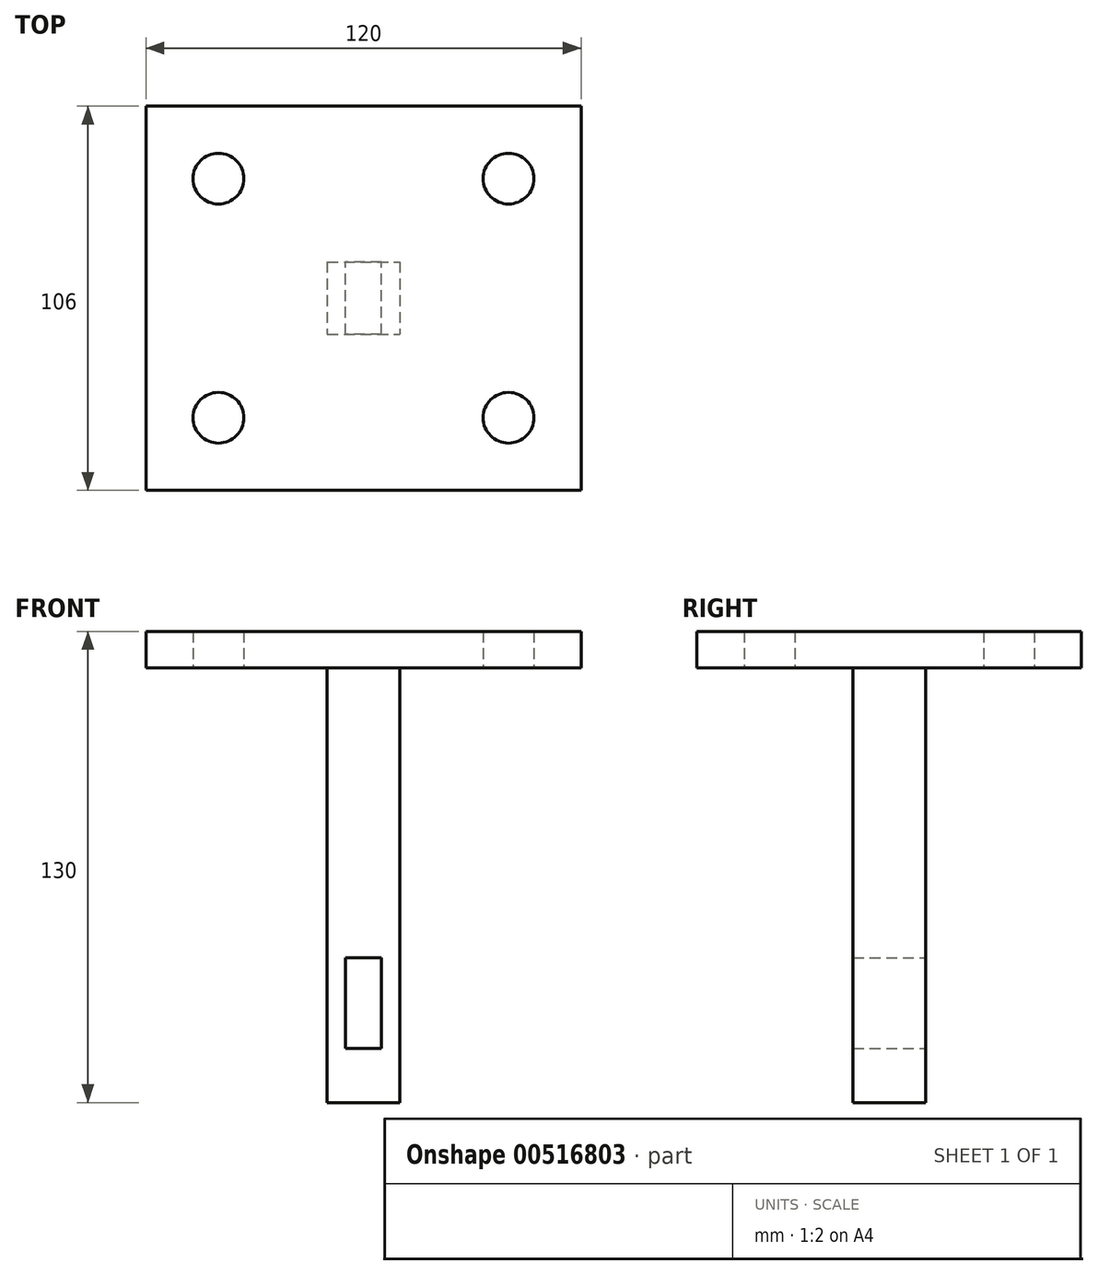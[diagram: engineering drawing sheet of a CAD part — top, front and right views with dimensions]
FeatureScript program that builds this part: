
annotation { "Feature Type Name" : "Feature", "Feature Type Description" : "" }
export const myFeature = defineFeature(function(context is Context, id is Id, definition is map)
    precondition{}
    {
        {
            var Q0;
            Q0=qCreatedBy(makeId("Top.planeOp"),FACE);
            var sketch = newSketch(context, id + "F0", { "sketchPlane" : qUnion([Q0])});
            skLineSegment(sketch, "E0.bottom", {"start": v(-60, 53) * mm, "end": v(60, 53) * mm});
            skLineSegment(sketch, "E0.top", {"start": v(-60, -53) * mm, "end": v(60, -53) * mm});
            skLineSegment(sketch, "E0.left", {"start": v(-60, 53) * mm, "end": v(-60, -53) * mm});
            skLineSegment(sketch, "E0.right", {"start": v(60, 53) * mm, "end": v(60, -53) * mm});
            skPoint(sketch, "E0.middle", {"position": v(0, 0) * mm});
            skLineSegment(sketch, "E1.bottom", {"start": v(-40, 33) * mm, "end": v(40, 33) * mm, "construction": true});
            skLineSegment(sketch, "E1.top", {"start": v(-40, -33) * mm, "end": v(40, -33) * mm, "construction": true});
            skLineSegment(sketch, "E1.left", {"start": v(-40, 33) * mm, "end": v(-40, -33) * mm, "construction": true});
            skLineSegment(sketch, "E1.right", {"start": v(40, 33) * mm, "end": v(40, -33) * mm, "construction": true});
            skCircle(sketch, "E2", {"center": v(-40, 33) * mm, "radius": 7 * mm});
            skCircle(sketch, "E3", {"center": v(-40, -33) * mm, "radius": 7 * mm});
            skCircle(sketch, "E4", {"center": v(40, -33) * mm, "radius": 7 * mm});
            skCircle(sketch, "E5", {"center": v(40, 33) * mm, "radius": 7 * mm});
            skLineSegment(sketch, "E6.bottom", {"start": v(-10, 10) * mm, "end": v(10, 10) * mm});
            skLineSegment(sketch, "E6.top", {"start": v(-10, -10) * mm, "end": v(10, -10) * mm});
            skLineSegment(sketch, "E6.left", {"start": v(-10, 10) * mm, "end": v(-10, -10) * mm});
            skLineSegment(sketch, "E6.right", {"start": v(10, 10) * mm, "end": v(10, -10) * mm});
            skSolve(sketch);
        }
        {
            var Q0;
            Q0=qCreatedBy(makeId("Front.planeOp"),FACE);
            var sketch = newSketch(context, id + "F1", { "sketchPlane" : qUnion([Q0])});
            skLineSegment(sketch, "E7.bottom", {"start": v(-5, -80) * mm, "end": v(5, -80) * mm});
            skLineSegment(sketch, "E7.top", {"start": v(-5, -105) * mm, "end": v(5, -105) * mm});
            skLineSegment(sketch, "E7.left", {"start": v(-5, -80) * mm, "end": v(-5, -105) * mm});
            skLineSegment(sketch, "E7.right", {"start": v(5, -80) * mm, "end": v(5, -105) * mm});
            skPoint(sketch, "E7.middle", {"position": v(0, -92.5) * mm});
            skSolve(sketch);
        }
        {
            var Q0;
            Q0=makeQuery(id+"F0.imprint","IMPRINT",FACE,{"disambiguationData":[TD([[makeQuery(id+"F0.imprint","IMPRINT",EDGE,{"derivedFrom":sQuery(id+"F0.wireOp",EDGE,"E6.bottom")}),-1.0]])]});
            extrude(context, id + "F2", {"entities" : qUnion([Q0]), "oppositeDirection" : true, "depth" : 120 * mm, "offsetDistance" : 25 * mm});
        }
        {
            var Q0;
            Q0=makeQuery(id+"F0.imprint","IMPRINT",FACE,{"disambiguationData":[TD([[makeQuery(id+"F0.imprint","IMPRINT",EDGE,{"derivedFrom":sQuery(id+"F0.wireOp",EDGE,"E0.bottom")}),-1.0]])]});
            var Q1;
            Q1=makeQuery(id+"F0.imprint","IMPRINT",FACE,{"disambiguationData":[TD([[makeQuery(id+"F0.imprint","IMPRINT",EDGE,{"derivedFrom":sQuery(id+"F0.wireOp",EDGE,"E6.bottom")}),-1.0]])]});
            extrude(context, id + "F3", {"entities" : qUnion([Q0, Q1]), "operationType" : NewBodyOperationType.ADD, "depth" : 10 * mm, "offsetDistance" : 25 * mm});
        }
        {
            var Q0;
            Q0 = qSketchRegion(id + "F1", true);
            extrude(context, id + "F4", {"entities" : qUnion([Q0]), "operationType" : NewBodyOperationType.REMOVE, "depth" : 25 * mm, "offsetDistance" : 25 * mm, "symmetric" : true});
        }
    });
